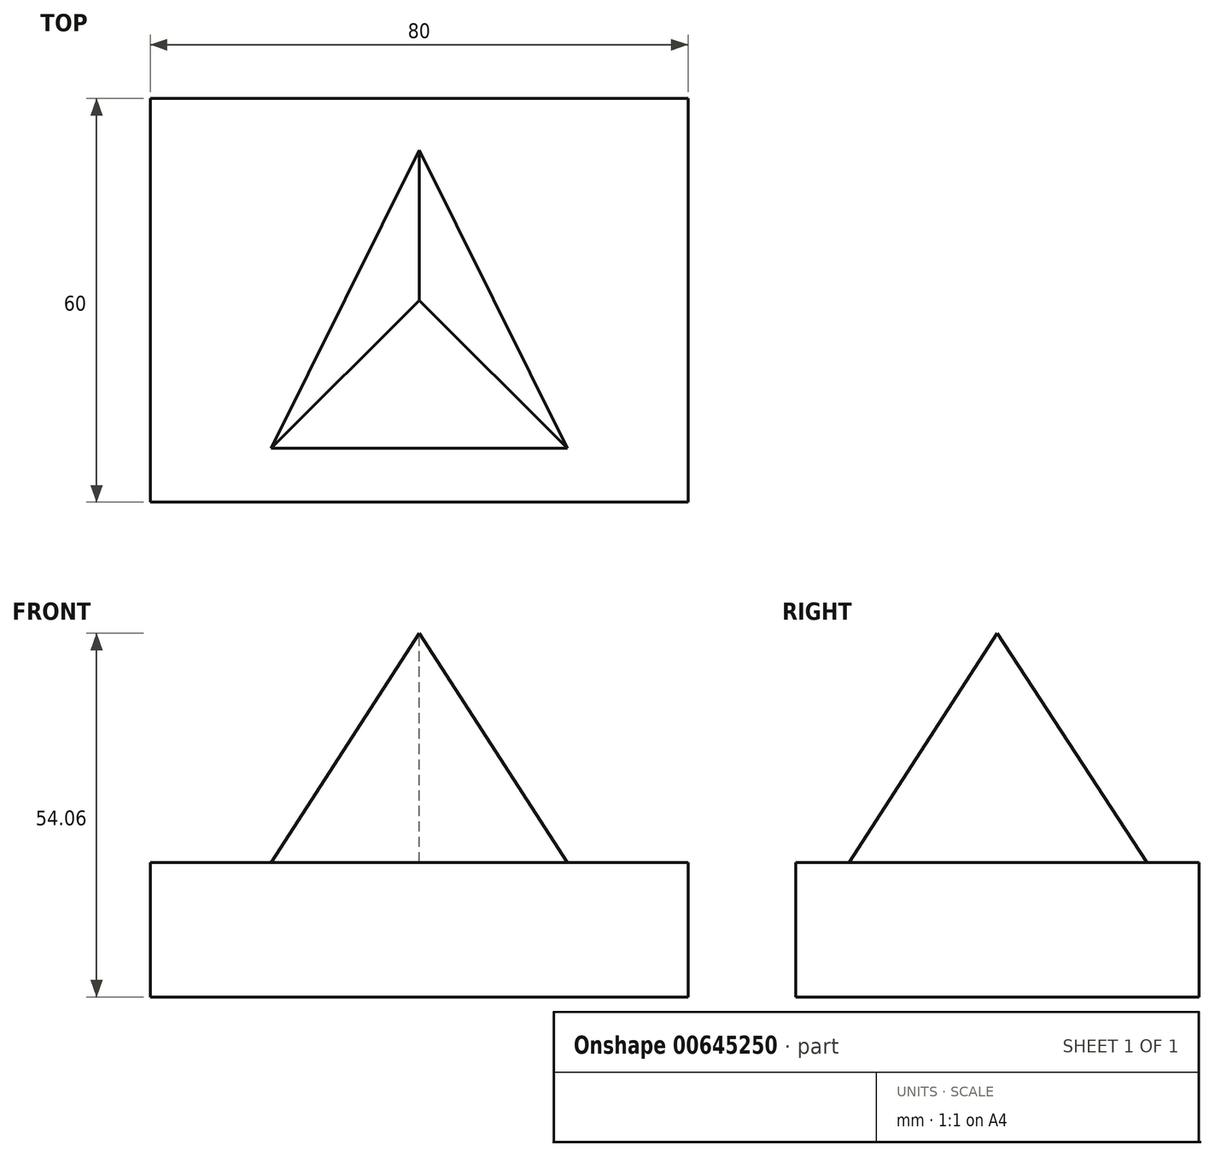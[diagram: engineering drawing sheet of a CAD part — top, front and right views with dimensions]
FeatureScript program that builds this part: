
annotation { "Feature Type Name" : "Feature", "Feature Type Description" : "" }
export const myFeature = defineFeature(function(context is Context, id is Id, definition is map)
    precondition{}
    {
        {
            var Q0;
            Q0=qCreatedBy(makeId("Top.planeOp"),FACE);
            var sketch = newSketch(context, id + "F0", { "sketchPlane" : qUnion([Q0])});
            skLineSegment(sketch, "E0.bottom", {"start": v(40, -30) * mm, "end": v(-40, -30) * mm});
            skLineSegment(sketch, "E0.top", {"start": v(40, 30) * mm, "end": v(-40, 30) * mm});
            skLineSegment(sketch, "E0.left", {"start": v(40, -30) * mm, "end": v(40, 30) * mm});
            skLineSegment(sketch, "E0.right", {"start": v(-40, -30) * mm, "end": v(-40, 30) * mm});
            skPoint(sketch, "E0.middle", {"position": v(0, 0) * mm});
            skSolve(sketch);
        }
        {
            var Q0;
            Q0 = qSketchRegion(id + "F0", true);
            extrude(context, id + "F1", {"entities" : qUnion([Q0]), "depth" : 20 * mm, "offsetDistance" : 25.4 * mm});
        }
        {
            var Q0;
            Q0=makeQuery(id+"F1.opExtrude","CAP_FACE",FACE,{"disambiguationData":[OSD([sQuery(id+"F0.wireOp",EDGE,"E0.bottom"),sQuery(id+"F0.wireOp",EDGE,"E0.top"),sQuery(id+"F0.wireOp",EDGE,"E0.left"),sQuery(id+"F0.wireOp",EDGE,"E0.right")])],"isStart":false});
            var sketch = newSketch(context, id + "F2", { "sketchPlane" : qUnion([Q0])});
            skLineSegment(sketch, "E1.bottom", {"start": v(-22.5, -22.5) * mm, "end": v(22.5, -22.5) * mm});
            skLineSegment(sketch, "E1.top", {"start": v(-22.5, 22.5) * mm, "end": v(22.5, 22.5) * mm});
            skLineSegment(sketch, "E1.left", {"start": v(-22.5, -22.5) * mm, "end": v(-22.5, 22.5) * mm});
            skLineSegment(sketch, "E1.right", {"start": v(22.5, -22.5) * mm, "end": v(22.5, 22.5) * mm});
            skPoint(sketch, "E1.middle", {"position": v(0, 0) * mm});
            skSolve(sketch);
        }
        {
            var Q0;
            Q0=makeQuery(id+"F2.imprint","IMPRINT",FACE,{"disambiguationData":[TD([[makeQuery(id+"F2.imprint","IMPRINT",EDGE,{"derivedFrom":sQuery(id+"F2.wireOp",EDGE,"E1.bottom")}),1.0]])]});
            var sketch = newSketch(context, id + "F3", { "sketchPlane" : qUnion([Q0])});
            skLineSegment(sketch, "E2", {"start": v(-22.02, -22.02) * mm, "end": v(0, 22.3) * mm});
            skLineSegment(sketch, "E3", {"start": v(0, 22.3) * mm, "end": v(0, -22.02) * mm});
            skLineSegment(sketch, "E4", {"start": v(0, -22.02) * mm, "end": v(-22.02, -22.02) * mm});
            skLineSegment(sketch, "E5.MirrorCS", {"start": v(22.02, -22.02) * mm, "end": v(0, 22.3) * mm});
            skLineSegment(sketch, "E6.MirrorCS", {"start": v(0, -22.02) * mm, "end": v(22.02, -22.02) * mm});
            skSolve(sketch);
        }
        {
            var Q0;
            Q0=qCreatedBy(makeId("Front.planeOp"),FACE);
            var sketch = newSketch(context, id + "F4", { "sketchPlane" : qUnion([Q0])});
            skLineSegment(sketch, "E7", {"start": v(0, 17.32) * mm, "end": v(0, 54.06) * mm});
            skSolve(sketch);
        }
        {
            var Q1;
            Q1 = qSketchRegion(id + "F3", true);
            var Q2;
            Q2=sQuery(id+"F4.wireOp",VERTEX,"E7.end");
            loft(context, id + "F5", {"operationType" : NewBodyOperationType.ADD, "sheetProfilesArray" : [{ "sheetProfileEntities" : qUnion([Q1]) }, { "sheetProfileEntities" : qUnion([Q2]) }]});
        }
    });
